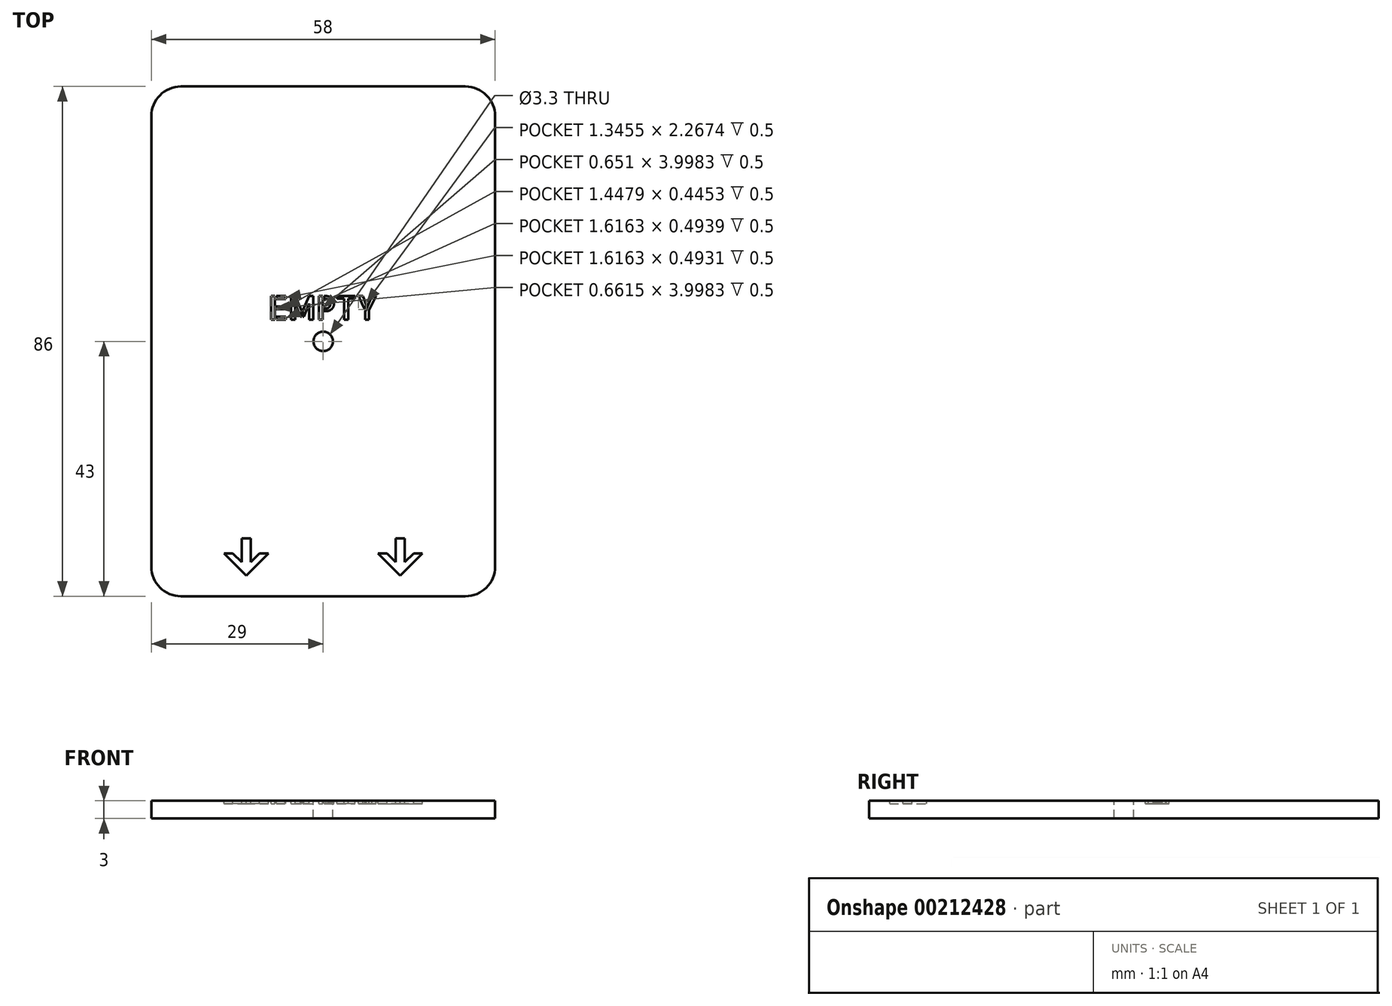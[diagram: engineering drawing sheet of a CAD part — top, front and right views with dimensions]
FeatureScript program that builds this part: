
annotation { "Feature Type Name" : "Feature", "Feature Type Description" : "" }
export const myFeature = defineFeature(function(context is Context, id is Id, definition is map)
    precondition{}
    {
        {
            var Q0;
            Q0=qCreatedBy(makeId("Top.planeOp"),FACE);
            var sketch = newSketch(context, id + "F0", { "sketchPlane" : qUnion([Q0])});
            skLineSegment(sketch, "E0.bottom", {"start": v(24, -43) * mm, "end": v(-24, -43) * mm});
            skLineSegment(sketch, "E0.top", {"start": v(24, 43) * mm, "end": v(-24, 43) * mm});
            skLineSegment(sketch, "E0.left", {"start": v(29, -38) * mm, "end": v(29, 38) * mm});
            skLineSegment(sketch, "E0.right", {"start": v(-29, -38) * mm, "end": v(-29, 38) * mm});
            skPoint(sketch, "E1.visualSharp", {"position": v(-29, 43) * mm});
            skArc(sketch, "E1.filletArc", {"start": v(-24, 43) * mm, "mid": v(-27.54, 41.54) * mm, "end": v(-29, 38) * mm});
            skPoint(sketch, "E2.visualSharp", {"position": v(29, 43) * mm});
            skArc(sketch, "E2.filletArc", {"start": v(29, 38) * mm, "mid": v(27.54, 41.54) * mm, "end": v(24, 43) * mm});
            skPoint(sketch, "E3.visualSharp", {"position": v(29, -43) * mm});
            skArc(sketch, "E3.filletArc", {"start": v(24, -43) * mm, "mid": v(27.54, -41.54) * mm, "end": v(29, -38) * mm});
            skPoint(sketch, "E4.visualSharp", {"position": v(-29, -43) * mm});
            skArc(sketch, "E4.filletArc", {"start": v(-29, -38) * mm, "mid": v(-27.54, -41.54) * mm, "end": v(-24, -43) * mm});
            skPoint(sketch, "E5", {"position": v(0, -43) * mm});
            skSolve(sketch);
        }
        {
            var Q0;
            Q0=makeQuery(id+"F0.imprint","IMPRINT",FACE,{"disambiguationData":[TD([[makeQuery(id+"F0.imprint","IMPRINT",EDGE,{"derivedFrom":sQuery(id+"F0.wireOp",EDGE,"E0.bottom")}),-1.0]])]});
            extrude(context, id + "F1", {"entities" : qUnion([Q0]), "depth" : 3 * mm});
        }
        {
            var Q0;
            Q0=makeQuery(id+"F1.opExtrude","CAP_FACE",FACE,{"disambiguationData":[OSD([sQuery(id+"F0.wireOp",EDGE,"E0.bottom"),sQuery(id+"F0.wireOp",EDGE,"E0.top"),sQuery(id+"F0.wireOp",EDGE,"E0.left"),sQuery(id+"F0.wireOp",EDGE,"E0.right"),sQuery(id+"F0.wireOp",EDGE,"E1.filletArc"),sQuery(id+"F0.wireOp",EDGE,"E2.filletArc"),sQuery(id+"F0.wireOp",EDGE,"E3.filletArc"),sQuery(id+"F0.wireOp",EDGE,"E4.filletArc"),sQuery(id+"F0.wireOp",EDGE,"ncc4mXFz-MKM4-u93i-xUpW-KqLA5N3EimXH"),sQuery(id+"F0.wireOp",EDGE,"V0mNEOgu-7ehB-mJIn-0MT6-GeH8bzEfoQNf"),sQuery(id+"F0.wireOp",EDGE,"ATUUKQ8d-FG66-FYUk-NJTq-WH9ksyN383sz"),sQuery(id+"F0.wireOp",EDGE,"51U2TfRn-3sMS-6mfT-S8zJ-HDxEAurlRJjI"),sQuery(id+"F0.wireOp",EDGE,"drJuF9Kv-lvIQ-y6Zv-Q0AP-lHh5Sw62L64L"),sQuery(id+"F0.wireOp",EDGE,"Y9EB5fiD-w1vB-GbbJ-39vz-p31e12hPuKoT"),sQuery(id+"F0.wireOp",EDGE,"lpWVEltg-yKk2-FC6Q-DWEt-GB9juuUDl7Lm"),sQuery(id+"F0.wireOp",EDGE,"bUbkZxVu-9vld-nzBv-8c3V-qy5McKLevpGz"),sQuery(id+"F0.wireOp",EDGE,"TtZAL4lW-ucmj-hyX8-PxtT-2QibSiqtMD5J"),sQuery(id+"F0.wireOp",EDGE,"Vn1urt2d-GUKl-KCpZ-l9H9-CVjlqKItf683"),sQuery(id+"F0.wireOp",EDGE,"HtFj1qPh-vI9O-y74d-NO1b-yT5N58iVD9pc"),sQuery(id+"F0.wireOp",EDGE,"1Zo0kP6v-pHMj-a3bH-940n-HKHA3xfrWGuD"),sQuery(id+"F0.wireOp",EDGE,"BbN0gsdK-qntY-4MKV-tvoa-ptIlF9A7BEeo"),sQuery(id+"F0.wireOp",EDGE,"kHtcMnSH-Ukyp-3z6O-Pww4-o2Yu0sv2seb1"),sQuery(id+"F0.wireOp",EDGE,"xRce3Ypx-Kg92-qRmD-ZxKj-G1UoRAdY27dX.bottom"),sQuery(id+"F0.wireOp",EDGE,"xRce3Ypx-Kg92-qRmD-ZxKj-G1UoRAdY27dX.top"),sQuery(id+"F0.wireOp",EDGE,"xRce3Ypx-Kg92-qRmD-ZxKj-G1UoRAdY27dX.left"),sQuery(id+"F0.wireOp",EDGE,"xRce3Ypx-Kg92-qRmD-ZxKj-G1UoRAdY27dX.right"),sQuery(id+"F0.wireOp",EDGE,"dbc4c125-c4bc-4e2f-b419-997c83cc6b2a.filletArc"),sQuery(id+"F0.wireOp",EDGE,"a0f7fecc-06a0-4b7f-b450-0e6330d459b2.filletArc"),sQuery(id+"F0.wireOp",EDGE,"dd6e476c-5c37-4b0e-8993-be78eb06bf35.filletArc"),sQuery(id+"F0.wireOp",EDGE,"b132e28a-0aab-47c1-8ebd-3aab864b6292.filletArc"),sQuery(id+"F0.wireOp",EDGE,"ZquWpEEf-0dOL-tgua-34wp-K6F6ahdsAqiY"),sQuery(id+"F0.wireOp",EDGE,"O9JaN2VC-ykhj-qAnB-Jd5I-Gmn6fEg3ICJQ"),sQuery(id+"F0.wireOp",EDGE,"AwmBYOTJ-LRbq-TWDU-Qy5A-Gqa55P9JIx6P"),sQuery(id+"F0.wireOp",EDGE,"gZRzCeEj-FGYz-o10X-BGuw-ZKnaBHhr3mMX")])],"isStart":false});
            var sketch = newSketch(context, id + "F2", { "sketchPlane" : qUnion([Q0])});
            skLineSegment(sketch, "E6", {"start": v(-13.75, -33.25) * mm, "end": v(-13.75, -37.25) * mm});
            skLineSegment(sketch, "E7", {"start": v(-13.75, -37.25) * mm, "end": v(-15.25, -35.75) * mm});
            skLineSegment(sketch, "E8", {"start": v(-15.25, -35.75) * mm, "end": v(-16.75, -35.75) * mm});
            skLineSegment(sketch, "E9", {"start": v(-16.75, -35.75) * mm, "end": v(-13, -39.5) * mm});
            skLineSegment(sketch, "E10", {"start": v(-13, -39.5) * mm, "end": v(-9.25, -35.75) * mm});
            skLineSegment(sketch, "E11", {"start": v(-9.25, -35.75) * mm, "end": v(-10.75, -35.75) * mm});
            skLineSegment(sketch, "E12", {"start": v(-10.75, -35.75) * mm, "end": v(-12.25, -37.25) * mm});
            skLineSegment(sketch, "E13", {"start": v(-12.25, -37.25) * mm, "end": v(-12.25, -33.25) * mm});
            skLineSegment(sketch, "E14", {"start": v(-12.25, -33.25) * mm, "end": v(-13.75, -33.25) * mm});
            skPoint(sketch, "E15", {"position": v(-13, -33.25) * mm});
            skLineSegment(sketch, "E16.MirrorCS", {"start": v(12.25, -33.25) * mm, "end": v(13.75, -33.25) * mm});
            skLineSegment(sketch, "E17.MirrorCS", {"start": v(12.25, -37.25) * mm, "end": v(12.25, -33.25) * mm});
            skLineSegment(sketch, "E18.MirrorCS", {"start": v(10.75, -35.75) * mm, "end": v(12.25, -37.25) * mm});
            skLineSegment(sketch, "E19.MirrorCS", {"start": v(9.25, -35.75) * mm, "end": v(10.75, -35.75) * mm});
            skLineSegment(sketch, "E20.MirrorCS", {"start": v(13, -39.5) * mm, "end": v(9.25, -35.75) * mm});
            skLineSegment(sketch, "E21.MirrorCS", {"start": v(16.75, -35.75) * mm, "end": v(13, -39.5) * mm});
            skLineSegment(sketch, "E22.MirrorCS", {"start": v(15.25, -35.75) * mm, "end": v(16.75, -35.75) * mm});
            skLineSegment(sketch, "E23.MirrorCS", {"start": v(13.75, -33.25) * mm, "end": v(13.75, -37.25) * mm});
            skLineSegment(sketch, "E24.MirrorCS", {"start": v(13.75, -37.25) * mm, "end": v(15.25, -35.75) * mm});
            skPoint(sketch, "E25.MirrorP", {"position": v(13, -33.25) * mm});
            skSolve(sketch);
        }
        {
            var Q0;
            Q0=qSketchRegion(id+"F2",true);
            extrude(context, id + "F3", {"entities" : qUnion([Q0]), "operationType" : NewBodyOperationType.REMOVE, "oppositeDirection" : true, "depth" : 0.5 * mm});
        }
        {
            var Q0;
            Q0=makeQuery(id+"F1.opExtrude","CAP_FACE",FACE,{"disambiguationData":[OSD([sQuery(id+"F0.wireOp",EDGE,"E0.bottom"),sQuery(id+"F0.wireOp",EDGE,"E0.top"),sQuery(id+"F0.wireOp",EDGE,"E0.left"),sQuery(id+"F0.wireOp",EDGE,"E0.right"),sQuery(id+"F0.wireOp",EDGE,"E1.filletArc"),sQuery(id+"F0.wireOp",EDGE,"E2.filletArc"),sQuery(id+"F0.wireOp",EDGE,"E3.filletArc"),sQuery(id+"F0.wireOp",EDGE,"E4.filletArc")])],"isStart":false});
            var sketch = newSketch(context, id + "F4", { "sketchPlane" : qUnion([Q0])});
            skCircle(sketch, "E26", {"center": v(0, 0) * mm, "radius": 1.65 * mm});
            skSolve(sketch);
        }
        {
            var Q0;
            Q0 = qSketchRegion(id + "F4", true);
            extrude(context, id + "F5", {"entities" : qUnion([Q0]), "operationType" : NewBodyOperationType.REMOVE, "endBound" : BoundingType.THROUGH_ALL, "oppositeDirection" : true, "depth" : 25 * mm});
        }
        {
            var Q0;
            Q0=makeQuery(id+"F1.opExtrude","CAP_FACE",FACE,{"disambiguationData":[OSD([sQuery(id+"F0.wireOp",EDGE,"E0.bottom"),sQuery(id+"F0.wireOp",EDGE,"E0.top"),sQuery(id+"F0.wireOp",EDGE,"E0.left"),sQuery(id+"F0.wireOp",EDGE,"E0.right"),sQuery(id+"F0.wireOp",EDGE,"E1.filletArc"),sQuery(id+"F0.wireOp",EDGE,"E2.filletArc"),sQuery(id+"F0.wireOp",EDGE,"E3.filletArc"),sQuery(id+"F0.wireOp",EDGE,"E4.filletArc")])],"isStart":false});
            var sketch = newSketch(context, id + "F6", { "sketchPlane" : qUnion([Q0])});
            skText(sketch, "E27", { "text": "EMPTY", "fontName": "AllertaStencil-Regular.ttf"});
            const initialGuessF6  = {"E27": [-0.00931, 0.00365, 1, 0, 0.004]};
            skSetInitialGuess(sketch, initialGuessF6);
            skSolve(sketch);
        }
        {
            var Q0;
            Q0 = qSketchRegion(id + "F6", true);
            extrude(context, id + "F7", {"entities" : qUnion([Q0]), "operationType" : NewBodyOperationType.REMOVE, "oppositeDirection" : true, "depth" : 0.5 * mm});
        }
    });
